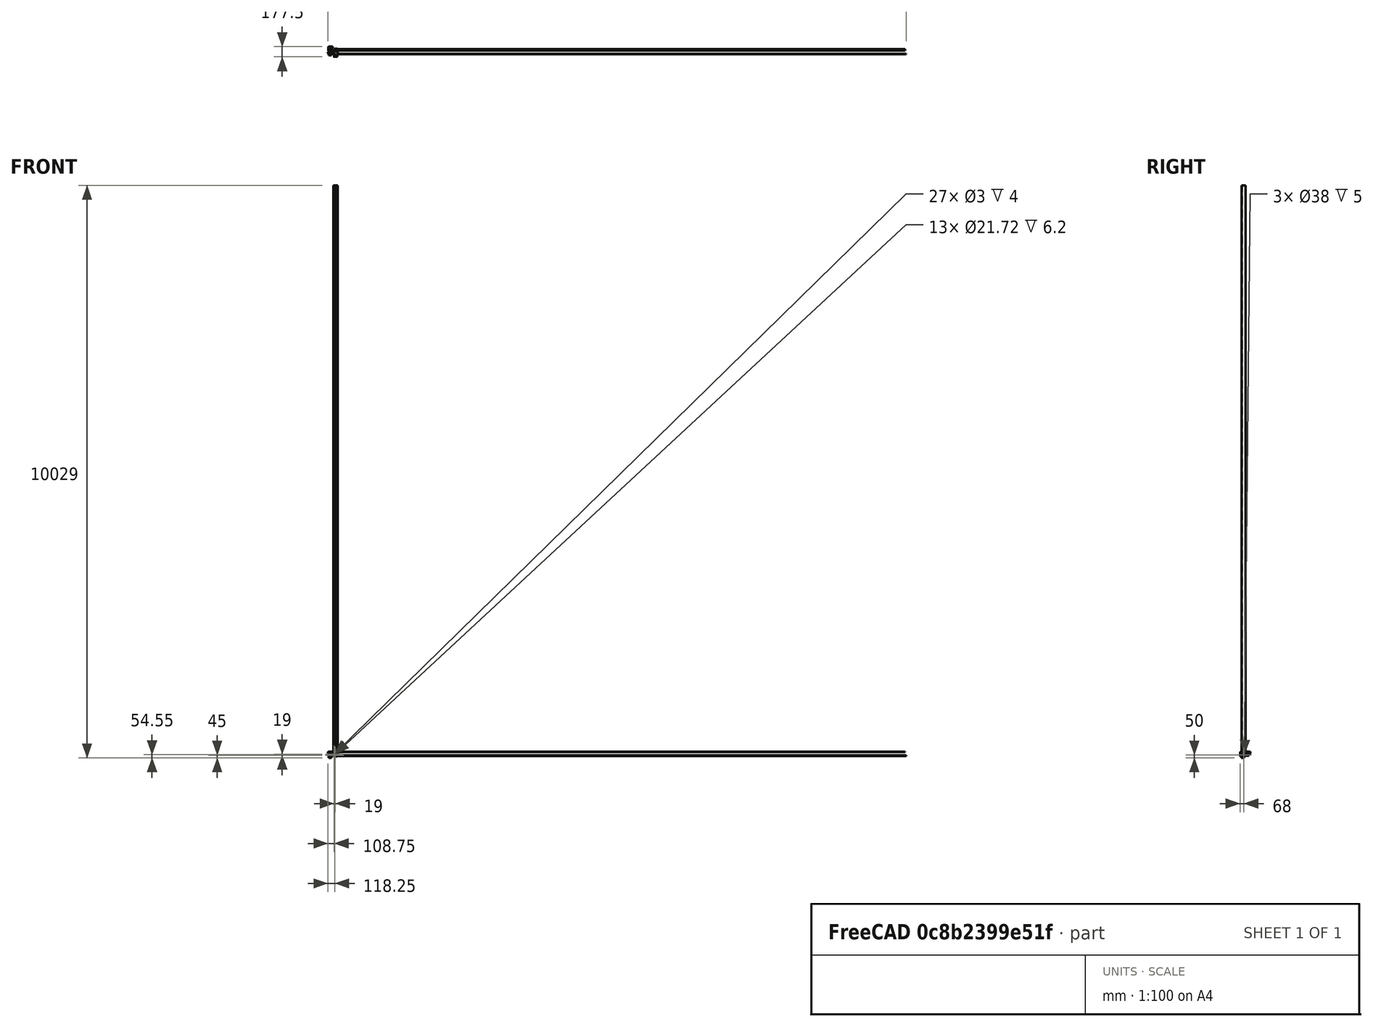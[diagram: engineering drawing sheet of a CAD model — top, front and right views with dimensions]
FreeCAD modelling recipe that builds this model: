
FCSTD DOCUMENT  (FreeCAD 0.15R4671 (Git))
Label: HexagonHotendFanShroud
License: All rights reserved
LicenseURL: http://en.wikipedia.org/wiki/All_rights_reserved
objects: Sketcher::SketchObject×30, Part::Feature×23, Mesh::Feature×20, PartDesign::Pocket×18, PartDesign::Pad×12, PartDesign::Fillet×10, Part::MultiFuse×1, PartDesign::Chamfer×1
note: 125 computed .brp shape members not serialized (recipe doc carries the construction recipe); baked Part::Feature solids carry a one-line shape summary decoded from their .brp

FEATURE [Part::Feature] Part__Feature  label="OB1515_45mm001"
  Placement = pos=(0,79.5,22.5) rot=(1,0,0;1.5708rad)
  shape: bbox 15 x 45 x 15 mm, 158 faces (baked)
FEATURE [Part::Feature] Part__Feature001  label="OB1515_45mm"
  Placement = pos=(7,93,-15) rot=(0,0,1;0.785398rad)
  shape: bbox 21.01 x 21.01 x 45 mm, 158 faces (baked)
FEATURE [Part::Feature] Part__Feature002  label="OB1515_45mm002"
  Placement = pos=(20.5,100,22.5) rot=(0.57735,0.57735,0.57735;2.0944rad)
  shape: bbox 45 x 15 x 15 mm, 158 faces (baked)
FEATURE [Part::Feature] Part__Feature003  label="NEMA17"
  Placement = pos=(36,64,2) rot=(0,0,1;0rad)
  shape: bbox 42.3 x 42.3 x 68 mm, 275 faces (baked)
FEATURE [Part::Feature] Part__Feature004  label="T5_Pulley"
  Placement = pos=(36,64,-4) rot=(0,0,1;0rad)
  shape: bbox 16 x 16 x 14.8 mm, 116 faces (baked)
FEATURE [Mesh::Feature] _08ZZ_Ball_Bearing  label="608ZZ_Ball_Bearing001"
  Placement = pos=(54.5,64,25.1) rot=(0,0,1;0rad)
FEATURE [Mesh::Feature] Spacer
  Placement = pos=(21.5,54,17.6) rot=(0,0,1;0rad)
FEATURE [Mesh::Feature] _mmRod_x100mm  label="8mmRod_x100mm"
  Placement = pos=(36,-64.5,-3.5) rot=(0,0,1;3.14159rad)
FEATURE [Part::Feature] Part__Feature005  label="TopCornerMotor"
  Placement = pos=(0,100,0) rot=(0,0,1;0rad)
  shape: bbox 69.55 x 77 x 28 mm, 82 faces (baked)
FEATURE [Part::Feature] Part__Feature006  label="TopRodHolder"
  Placement = pos=(0,100,2) rot=(0,0,1;0rad)
  shape: bbox 30.16 x 11.33 x 11.99 mm, 58 faces (baked)
FEATURE [Part::Feature] LM8UU_8mm_Linear_Bearing001
  Placement = pos=(36,-24.5,-3.5) rot=(0,0,1;1.5708rad)
  shape: bbox 15 x 24 x 15 mm, 34 faces (baked)
FEATURE [Mesh::Feature] _mmRod_x100mm001  label="8mmRod_x100mm001"
  Placement = pos=(66,7.5,1.5) rot=(0,0,1;1.5708rad)
FEATURE [Mesh::Feature] _mmRod_x100mm002  label="8mmRod_x100mm002"
  Placement = pos=(66,-32.5,1.5) rot=(0,0,1;1.5708rad)
FEATURE [Mesh::Feature] _0mmFan  label="40mmFan"
  Placement = pos=(102,-18,-36) rot=(-1,0,0;1.5708rad)
FEATURE [Mesh::Feature] HexHotEnd  label="HexHotEnd1"
  Placement = pos=(104,-57,-34) rot=(0,0,1;0rad)
FEATURE [Mesh::Feature] PNEUMATIC_NIPPLE
  Placement = pos=(111,-66,-3) rot=(0,-1,0;1.5708rad)
FEATURE [Part::Feature] Part__Feature015  label="AluAngle"
  Placement = pos=(0,5,-80) rot=(-1,0,0;1.5708rad)
  shape: bbox 50 x 50.8 x 50.8 mm, 9 faces (baked)
FEATURE [Mesh::Feature] _x10x4_FlangedBearing  label="5x10x4_FlangedBearing_BOTTOM"
  Placement = pos=(49,-6,16) rot=(-1,0,0;1.5708rad)
FEATURE [Mesh::Feature] _x10x4_FlangedBearing001  label="5x10x4_FlangedBearing_TOP"
  Placement = pos=(49,-6,12) rot=(1,0,0;1.5708rad)
FEATURE [Mesh::Feature] _x10x4_FlangedBearing002  label="5x10x4_FlangedBearing_BOTTOM001"
  Placement = pos=(49,-19,16) rot=(-1,0,0;1.5708rad)
FEATURE [Mesh::Feature] _x10x4_FlangedBearing003  label="5x10x4_FlangedBearing_TOP001"
  Placement = pos=(49,-19,12) rot=(1,0,0;1.5708rad)
FEATURE [Part::Feature] Part__Feature016  label="XCarrageBeltBlock"
  Placement = pos=(9,0,0) rot=(0,0,1;0rad)
  shape: bbox 56 x 22 x 10 mm, 113 faces (baked)
FEATURE [Part::Feature] Part__Feature017  label="LJ18A3"
  Placement = pos=(136,-57,-52) rot=(0,0,1;0rad)
  shape: bbox 17.85 x 17.85 x 79.1 mm, 11 faces (baked)
FEATURE [Mesh::Feature] HexNutStyle1_M002  label="HexNutStyle1_M006"
  Placement = pos=(50.3,7.15,-114) rot=(0,0,1;0.523599rad)
FEATURE [Mesh::Feature] HexNutStyle1_M003  label="HexNutStyle1_M007"
  Placement = pos=(50.3,20.15,-114) rot=(0,0,1;0.523599rad)
FEATURE [Part::Feature] Part__Feature018  label="YCarrage"
  shape: bbox 34.23 x 25.99 x 62.01 mm, 85 faces (baked)
FEATURE [Part::Feature] LM8UU_8mm_Linear_Bearing
  Placement = pos=(95,7.5,1.5) rot=(-1,0,0;1.5708rad)
  shape: bbox 24 x 15 x 15 mm, 34 faces (baked)
FEATURE [Part::Feature] LM8UU_8mm_Linear_Bearing002
  Placement = pos=(95,-32.5,1.5) rot=(-1,0,0;1.5708rad)
  shape: bbox 24 x 15 x 15 mm, 34 faces (baked)
FEATURE [Part::Feature] LM8UU_8mm_Linear_Bearing003
  Placement = pos=(123,7.5,1.5) rot=(-1,0,0;1.5708rad)
  shape: bbox 24 x 15 x 15 mm, 34 faces (baked)
FEATURE [Part::Feature] LM8UU_8mm_Linear_Bearing004
  Placement = pos=(123,-32.5,1.5) rot=(-1,0,0;1.5708rad)
  shape: bbox 24 x 15 x 15 mm, 34 faces (baked)
FEATURE [Mesh::Feature] MicroSwitch
  Placement = pos=(99,-12.5,-5) rot=(0,0,1;1.5708rad)
FEATURE [Part::Feature] Part__Feature019  label="XCarrageTop"
  shape: bbox 56 x 70.62 x 16.52 mm, 278 faces (baked)
FEATURE [Part::Feature] Part__Feature020  label="ChinaBlowerFan"
  shape: bbox 33.55 x 33.55 x 13 mm, 169 faces (baked)
FEATURE [Part::Feature] Part__Feature021  label="ChinaBlowerFan001"
  shape: bbox 40.62 x 40.6 x 19.6 mm, 81 faces (baked)
FEATURE [Part::MultiFuse] Fusion  label="ChinaBlowerFan002"
  Placement = pos=(114,-4,-13) rot=(0.707107,0.707107,0;3.14159rad)
  Shapes = -> [Part__Feature020,Part__Feature021]
FEATURE [Mesh::Feature] _0mmFan001  label="40mmFan001"
  Placement = pos=(141,-1,-23) rot=(0.57735,-0.57735,0.57735;4.18879rad)
FEATURE [Mesh::Feature] ALIEXPRESS_Aluhotend40mmFan
FEATURE [Mesh::Feature] Fan_25mm_x_10mm
  Placement = pos=(105.5,-31,-25.5) rot=(0,0.707107,0.707107;3.14159rad)
FEATURE [Mesh::Feature] HexHotEnd2
  Placement = pos=(104,-57,-34) rot=(0,0,1;0rad)
FEATURE [Part::Feature] Part__Feature022  label="Hexagon fanshroud"
  shape: bbox 25.5 x 25.5 x 18 mm, 35 faces (baked)
FEATURE [Mesh::Feature] hexagon_fan
  Placement = pos=(198.15,-46.7,56) rot=(0.57735,-0.57735,0.57735;2.0944rad)
FEATURE [Part::Feature] Part__Feature023  label="TempXCarrageBottom"
  shape: bbox 57.67 x 88 x 16.5 mm, 58 faces (baked)
FEATURE [Sketcher::SketchObject] Sketch
  Placement = pos=(0,0,-10.2) rot=(1,0,0;3.14159rad)
  sketch-geometry (4):
    g0: LineSegment StartX=93 StartY=70 StartZ=0 EndX=149 EndY=70 EndZ=0
    g1: LineSegment StartX=149 StartY=70 StartZ=0 EndX=149 EndY=-18 EndZ=0
    g2: LineSegment StartX=149 StartY=-18 StartZ=0 EndX=93 EndY=-18 EndZ=0
    g3: LineSegment StartX=93 StartY=-18 StartZ=0 EndX=93 EndY=70 EndZ=0
  constraints (8):
    c: Coincident(g0,g1)
    c: Coincident(g1,g2)
    c: Coincident(g2,g3)
    c: Coincident(g3,g0)
    c: Horizontal(g0)
    c: Horizontal(g2)
    c: Vertical(g1)
    c: Vertical(g3)
FEATURE [PartDesign::Pad] Pad
  Length = 3
  Length2 = 100
  Placement = pos=(0,0,-10.2) rot=(1,0,0;3.14159rad)
  Sketch = -> Sketch
  Type = 0
FEATURE [Sketcher::SketchObject] Sketch001
  Placement = pos=(0,0,-13.2) rot=(1,0,0;3.14159rad)
  Support = -> Pad [Face6]
  sketch-geometry (11):
    g0: LineSegment StartX=93 StartY=36 StartZ=0 EndX=118 EndY=36 EndZ=0
    g1: LineSegment StartX=118 StartY=36 StartZ=0 EndX=118 EndY=41 EndZ=0
    g2: LineSegment StartX=118 StartY=41 StartZ=0 EndX=114.5 EndY=62 EndZ=0
    g3: LineSegment StartX=93.5 StartY=62 StartZ=0 EndX=93 EndY=41 EndZ=0
    g4: LineSegment StartX=93 StartY=41 StartZ=0 EndX=93 EndY=36 EndZ=0
    g5: LineSegment StartX=114.5 StartY=62 StartZ=0 EndX=113 EndY=62 EndZ=0
    g6: LineSegment StartX=113 StartY=62 StartZ=0 EndX=113 EndY=52 EndZ=0
    g7: LineSegment StartX=113 StartY=52 StartZ=0 EndX=104 EndY=47 EndZ=0
    g8: LineSegment StartX=104 StartY=47 StartZ=0 EndX=95 EndY=52 EndZ=0
    g9: LineSegment StartX=95 StartY=52 StartZ=0 EndX=95 EndY=62 EndZ=0
    g10: LineSegment StartX=95 StartY=62 StartZ=0 EndX=93.5 EndY=62 EndZ=0
  constraints (16):
    c: Horizontal(g0)
    c: Coincident(g0,g1)
    c: Coincident(g1,g2)
    c: Coincident(g3,g4)
    c: Coincident(g4,g0)
    c: Coincident(g2,g5)
    c: Horizontal(g5)
    c: Coincident(g5,g6)
    c: Vertical(g6)
    c: Coincident(g6,g7)
    c: Coincident(g7,g8)
    c: Coincident(g8,g9)
    c: Vertical(g9)
    c: Coincident(g9,g10)
    c: Coincident(g10,g3)
    c: Horizontal(g10)
FEATURE [PartDesign::Pad] Pad001
  Length = 24.5
  Length2 = 100
  Placement = pos=(0,0,-10.2) rot=(1,0,0;3.14159rad)
  Sketch = -> Sketch001
  Type = 0
FEATURE [Sketcher::SketchObject] Sketch002
  Placement = pos=(93,0,-10.2) rot=(0.57735,0.57735,-0.57735;4.18879rad)
  Support = -> Pad001 [Face17]
  sketch-geometry (6):
    g0: LineSegment StartX=-63 StartY=23.5 StartZ=0 EndX=-62 EndY=23.5 EndZ=0
    g1: LineSegment StartX=-62 StartY=23.5 StartZ=0 EndX=-47 EndY=23.5 EndZ=0
    g2: LineSegment StartX=-47 StartY=23.5 StartZ=0 EndX=-41 EndY=25.5 EndZ=0
    g3: LineSegment StartX=-41 StartY=25.5 StartZ=0 EndX=-41 EndY=28 EndZ=0
    g4: LineSegment StartX=-41 StartY=28 StartZ=0 EndX=-63 EndY=28 EndZ=0
    g5: LineSegment StartX=-63 StartY=28 StartZ=0 EndX=-63 EndY=23.5 EndZ=0
  constraints (11):
    c: Horizontal(g0)
    c: Coincident(g0,g1)
    c: Horizontal(g1)
    c: Coincident(g1,g2)
    c: Coincident(g2,g3)
    c: Vertical(g3)
    c: Coincident(g3,g4)
    c: Horizontal(g4)
    c: Coincident(g4,g5)
    c: Coincident(g5,g0)
    c: Vertical(g5)
FEATURE [PartDesign::Pocket] Pocket
  Length = 5
  Placement = pos=(0,0,-10.2) rot=(1,0,0;3.14159rad)
  Sketch = -> Sketch002
  Type = 1
FEATURE [Sketcher::SketchObject] Sketch003
  Placement = pos=(0,-36,-10.2) rot=(-1,0,0;1.5708rad)
  Support = -> Pocket [Face7]
  sketch-geometry (1):
    g0: Circle CenterX=105.5 CenterY=15.25 CenterZ=0 NormalX=0 NormalY=0 NormalZ=1 Radius=10.8605
FEATURE [PartDesign::Pocket] Pocket001
  Length = 3
  Placement = pos=(0,0,-10.2) rot=(1,0,0;3.14159rad)
  Sketch = -> Sketch003
  Type = 0
FEATURE [Sketcher::SketchObject] Sketch004
  Placement = pos=(0,0,-10.2) rot=(0,0,1;0rad)
  Support = -> Pocket001 [Face4]
  sketch-geometry (7):
    g0: LineSegment StartX=94.75 StartY=-70.5 StartZ=0 EndX=94.75 EndY=-38.75 EndZ=0
    g1: LineSegment StartX=94.75 StartY=-38.75 StartZ=0 EndX=116.25 EndY=-38.75 EndZ=0
    g2: LineSegment StartX=116.25 StartY=-38.75 StartZ=0 EndX=116.5 EndY=-39 EndZ=0
    g3: LineSegment StartX=116.5 StartY=-39 StartZ=0 EndX=116.5 EndY=-41 EndZ=0
    g4: LineSegment StartX=116.5 StartY=-41 StartZ=0 EndX=113 EndY=-62 EndZ=0
    g5: LineSegment StartX=113 StartY=-62 StartZ=0 EndX=113 EndY=-70.5 EndZ=0
    g6: LineSegment StartX=113 StartY=-70.5 StartZ=0 EndX=94.75 EndY=-70.5 EndZ=0
  constraints (12):
    c: Vertical(g0)
    c: Horizontal(g1)
    c: Coincident(g1,g2)
    c: Coincident(g2,g3)
    c: Vertical(g3)
    c: Coincident(g3,g4)
    c: Coincident(g4,g5)
    c: Vertical(g5)
    c: Coincident(g5,g6)
    c: Horizontal(g6)
    c: Coincident(g0,g6)
    c: Coincident(g0,g1)
FEATURE [PartDesign::Pocket] Pocket002
  Length = 22.8
  Placement = pos=(0,0,-10.2) rot=(1,0,0;3.14159rad)
  Sketch = -> Sketch004
  Type = 0
FEATURE [PartDesign::Chamfer] Chamfer
  Base = -> Pocket002 [Edge60]
  Placement = pos=(0,0,-10.2) rot=(1,0,0;3.14159rad)
  Size = 3.2
FEATURE [PartDesign::Fillet] Fillet
  Base = -> Chamfer [Edge86,Edge76]
  Placement = pos=(0,0,-10.2) rot=(1,0,0;3.14159rad)
  Radius = 2
FEATURE [Sketcher::SketchObject] Sketch005
  Placement = pos=(0,0,-13.2) rot=(1,0,0;3.14159rad)
  Support = -> Fillet [Face4]
  sketch-geometry (8):
    g0: LineSegment StartX=92.5 StartY=41 StartZ=0 EndX=93.5 EndY=41 EndZ=0
    g1: LineSegment StartX=93.5 StartY=41 StartZ=0 EndX=93.5 EndY=62 EndZ=0
    g2: LineSegment StartX=93.5 StartY=62 StartZ=0 EndX=114.5 EndY=62 EndZ=0
    g3: LineSegment StartX=114.5 StartY=62 StartZ=0 EndX=118 EndY=41 EndZ=0
    g4: LineSegment StartX=118 StartY=41 StartZ=0 EndX=149.5 EndY=41 EndZ=0
    g5: LineSegment StartX=149.5 StartY=41 StartZ=0 EndX=149.5 EndY=70.25 EndZ=0
    g6: LineSegment StartX=149.5 StartY=70.25 StartZ=0 EndX=92.5 EndY=70.25 EndZ=0
    g7: LineSegment StartX=92.5 StartY=70.25 StartZ=0 EndX=92.5 EndY=41 EndZ=0
  constraints (14):
    c: Horizontal(g0)
    c: Coincident(g0,g1)
    c: Vertical(g1)
    c: Coincident(g1,g2)
    c: Horizontal(g2)
    c: Coincident(g2,g3)
    c: Coincident(g3,g4)
    c: Horizontal(g4)
    c: Coincident(g4,g5)
    c: Vertical(g5)
    c: Coincident(g5,g6)
    c: Horizontal(g6)
    c: Coincident(g6,g7)
    c: Coincident(g7,g0)
FEATURE [PartDesign::Pocket] Pocket003
  Length = 5
  Placement = pos=(0,0,-10.2) rot=(1,0,0;3.14159rad)
  Sketch = -> Sketch005
  Type = 0
FEATURE [Sketcher::SketchObject] Sketch006
  Placement = pos=(0,0,-10.2) rot=(0,0,1;0rad)
  Support = -> Pocket003 [Face11]
  sketch-geometry (7):
    g0: LineSegment StartX=93 StartY=-38.25 StartZ=0 EndX=93 EndY=-41 EndZ=0
    g1: LineSegment StartX=93 StartY=-41 StartZ=0 EndX=93.5 EndY=-62 EndZ=0
    g2: LineSegment StartX=93.5 StartY=-62 StartZ=0 EndX=94 EndY=-62 EndZ=0
    g3: LineSegment StartX=94 StartY=-62 StartZ=0 EndX=94 EndY=-44.25 EndZ=0
    g4: LineSegment StartX=94 StartY=-44.25 StartZ=0 EndX=116.75 EndY=-44.25 EndZ=0
    g5: LineSegment StartX=116.75 StartY=-44.25 StartZ=0 EndX=116.75 EndY=-38.25 EndZ=0
    g6: LineSegment StartX=116.75 StartY=-38.25 StartZ=0 EndX=93 EndY=-38.25 EndZ=0
  constraints (12):
    c: Vertical(g0)
    c: Coincident(g0,g1)
    c: Coincident(g1,g2)
    c: Horizontal(g2)
    c: Coincident(g2,g3)
    c: Coincident(g3,g4)
    c: Horizontal(g4)
    c: Coincident(g4,g5)
    c: Vertical(g5)
    c: Coincident(g5,g6)
    c: Horizontal(g6)
    c: Coincident(g0,g6)
FEATURE [PartDesign::Pad] Pad002
  Length = 3
  Length2 = 100
  Placement = pos=(0,0,-10.2) rot=(1,0,0;3.14159rad)
  Reversed = true
  Sketch = -> Sketch006
  Type = 0
FEATURE [Part::Feature] Pad002001  label="Pad003"
  shape: bbox 56 x 80 x 27.5 mm, 37 faces (baked)
FEATURE [Sketcher::SketchObject] Sketch007
  Placement = pos=(0,0,-13.2) rot=(1,0,0;3.14159rad)
  Support = -> Pad002001 [Face32]
  sketch-geometry (2):
    g0: Circle CenterX=107 CenterY=44.25 CenterZ=0 NormalX=0 NormalY=0 NormalZ=1 Radius=1.8
    g1: Circle CenterX=107 CenterY=44.25 CenterZ=0 NormalX=0 NormalY=0 NormalZ=1 Radius=3.25
  constraints (2):
    c: Radius(g0) = 1.8
    c: Coincident(g1,g0)
FEATURE [PartDesign::Pad] Pad002002
  Length = 3
  Length2 = 100
  Reversed = true
  Sketch = -> Sketch007
  Type = 0
FEATURE [Sketcher::SketchObject] Sketch008
  Placement = pos=(0,0,-13.2) rot=(1,0,0;3.14159rad)
  Support = -> Pad002002 [Face38]
  sketch-geometry (1):
    g0: Circle CenterX=107 CenterY=44.25 CenterZ=0 NormalX=0 NormalY=0 NormalZ=1 Radius=1.81
  constraints (1):
    c: Radius(g0) = 1.81
FEATURE [PartDesign::Pocket] Pocket004
  Length = 4
  Sketch = -> Sketch008
  Type = 0
FEATURE [PartDesign::Fillet] Fillet001
  Base = -> Pocket004 [Edge109,Edge105]
  Radius = 3
FEATURE [PartDesign::Fillet] Fillet002
  Base = -> Fillet001 [Edge42,Edge20]
  Radius = 2
FEATURE [Sketcher::SketchObject] Sketch009
  Placement = pos=(0,-36,0) rot=(0,0.707107,0.707107;3.14159rad)
  Support = -> Fillet002 [Face34]
  sketch-geometry (4):
    g0: Circle CenterX=-115 CenterY=-16 CenterZ=0 NormalX=0 NormalY=0 NormalZ=1 Radius=1.5
    g1: Circle CenterX=-96 CenterY=-16 CenterZ=0 NormalX=0 NormalY=0 NormalZ=1 Radius=1.5
    g2: Circle CenterX=-96 CenterY=-35 CenterZ=0 NormalX=0 NormalY=0 NormalZ=1 Radius=1.5
    g3: Circle CenterX=-115 CenterY=-35 CenterZ=0 NormalX=0 NormalY=0 NormalZ=1 Radius=1.5
  constraints (4):
    c: Radius(g0) = 1.5
    c: Radius(g1) = 1.5
    c: Radius(g2) = 1.5
    c: Radius(g3) = 1.5
FEATURE [PartDesign::Pocket] Pocket005
  Length = 4
  Sketch = -> Sketch009
  Type = 0
FEATURE [Sketcher::SketchObject] Sketch011
  Placement = pos=(0,0,-13.2) rot=(1,0,0;3.14159rad)
  Support = -> Pocket005 [Face27]
  sketch-geometry (4):
    g0: LineSegment StartX=138 StartY=-18 StartZ=0 EndX=134 EndY=-18 EndZ=0
    g1: LineSegment StartX=134 StartY=-18 StartZ=0 EndX=134 EndY=22 EndZ=0
    g2: LineSegment StartX=134 StartY=22 StartZ=0 EndX=138 EndY=22 EndZ=0
    g3: LineSegment StartX=138 StartY=22 StartZ=0 EndX=138 EndY=-18 EndZ=0
  constraints (8):
    c: Coincident(g0,g1)
    c: Coincident(g1,g2)
    c: Coincident(g2,g3)
    c: Coincident(g3,g0)
    c: Horizontal(g0)
    c: Horizontal(g2)
    c: Vertical(g1)
    c: Vertical(g3)
FEATURE [PartDesign::Pad] Pad002003
  Length = 37
  Length2 = 100
  Sketch = -> Sketch011
  Type = 0
FEATURE [Sketcher::SketchObject] Sketch012
  Placement = pos=(138,0,0) rot=(0.57735,0.57735,0.57735;2.0944rad)
  Support = -> Pad002003 [Face45]
  sketch-geometry (1):
    g0: Circle CenterX=-2 CenterY=-30 CenterZ=0 NormalX=0 NormalY=0 NormalZ=1 Radius=19
  constraints (1):
    c: Radius(g0) = 19
FEATURE [PartDesign::Pocket] Pocket006
  Length = 5
  Sketch = -> Sketch012
  Type = 0
FEATURE [Sketcher::SketchObject] Sketch013
  Placement = pos=(0,18,0) rot=(0,0.707107,0.707107;3.14159rad)
  Support = -> Pocket006 [Face15]
  sketch-geometry (6):
    g0: LineSegment StartX=-135 StartY=-50 StartZ=0 EndX=-93 EndY=-50 EndZ=0
    g1: LineSegment StartX=-93 StartY=-50 StartZ=0 EndX=-93 EndY=-39 EndZ=0
    g2: LineSegment StartX=-135 StartY=-12 StartZ=0 EndX=-135 EndY=-50 EndZ=0
    g3: LineSegment StartX=-93 StartY=-39 StartZ=0 EndX=-120 EndY=-39 EndZ=0
    g4: LineSegment StartX=-120 StartY=-39 StartZ=0 EndX=-126 EndY=-12 EndZ=0
    g5: LineSegment StartX=-126 StartY=-12 StartZ=0 EndX=-135 EndY=-12 EndZ=0
  constraints (11):
    c: Coincident(g0,g1)
    c: Coincident(g2,g0)
    c: Horizontal(g0)
    c: Vertical(g1)
    c: Vertical(g2)
    c: Coincident(g1,g3)
    c: Horizontal(g3)
    c: Coincident(g3,g4)
    c: Coincident(g4,g5)
    c: Horizontal(g5)
    c: Coincident(g2,g5)
FEATURE [PartDesign::Pad] Pad002004
  Length = 40
  Length2 = 100
  Reversed = true
  Sketch = -> Sketch013
  Type = 0
FEATURE [Sketcher::SketchObject] Sketch014
  Placement = pos=(93,0,0) rot=(0.57735,-0.57735,-0.57735;2.0944rad)
  Support = -> Pad002004 [Face57]
  sketch-geometry (5):
    g0: LineSegment StartX=24 StartY=-51.2126 StartZ=0 EndX=24 EndY=-41 EndZ=0
    g1: LineSegment StartX=24 StartY=-41 StartZ=0 EndX=22 EndY=-41 EndZ=0
    g2: LineSegment StartX=22 StartY=-41 StartZ=0 EndX=17 EndY=-50.2195 EndZ=0
    g3: LineSegment StartX=17 StartY=-50.2195 StartZ=0 EndX=17 EndY=-51.2126 EndZ=0
    g4: LineSegment StartX=17 StartY=-51.2126 StartZ=0 EndX=24 EndY=-51.2126 EndZ=0
  constraints (9):
    c: Vertical(g0)
    c: Coincident(g0,g1)
    c: Horizontal(g1)
    c: Coincident(g1,g2)
    c: Coincident(g2,g3)
    c: Vertical(g3)
    c: Coincident(g3,g4)
    c: Coincident(g4,g0)
    c: Horizontal(g4)
FEATURE [PartDesign::Pocket] Pocket007
  Length = 5
  Sketch = -> Sketch014
  Type = 1
FEATURE [PartDesign::Fillet] Fillet003
  Base = -> Pocket007 [Edge73]
  Radius = 25
FEATURE [Sketcher::SketchObject] Sketch015
  Placement = pos=(93,0,0) rot=(0.57735,-0.57735,-0.57735;2.0944rad)
  Support = -> Fillet003 [Face13]
  sketch-geometry (4):
    g0: LineSegment StartX=-21.7137 StartY=-49 StartZ=0 EndX=26 EndY=-49 EndZ=0
    g1: LineSegment StartX=26 StartY=-49 StartZ=0 EndX=26 EndY=-52 EndZ=0
    g2: LineSegment StartX=26 StartY=-52 StartZ=0 EndX=-21.7137 EndY=-52 EndZ=0
    g3: LineSegment StartX=-21.7137 StartY=-52 StartZ=0 EndX=-21.7137 EndY=-49 EndZ=0
  constraints (8):
    c: Coincident(g0,g1)
    c: Coincident(g1,g2)
    c: Coincident(g2,g3)
    c: Coincident(g3,g0)
    c: Horizontal(g0)
    c: Horizontal(g2)
    c: Vertical(g1)
    c: Vertical(g3)
FEATURE [PartDesign::Pocket] Pocket008
  Length = 41
  Sketch = -> Sketch015
  Type = 0
FEATURE [Sketcher::SketchObject] Sketch016
  Placement = pos=(0,0,-49) rot=(1,0,0;3.14159rad)
  Support = -> Pocket008 [Face2]
  sketch-geometry (5):
    g0: ArcOfCircle CenterX=117.001 CenterY=6 CenterZ=0 NormalX=0 NormalY=0 NormalZ=1 Radius=21.0014 StartAngle=3.14159 EndAngle=4.72394
    g1: LineSegment StartX=96 StartY=6 StartZ=0 EndX=96 EndY=23.1942 EndZ=0
    g2: LineSegment StartX=96 StartY=23.1942 StartZ=0 EndX=134 EndY=23.1942 EndZ=0
    g3: LineSegment StartX=134 StartY=23.1942 StartZ=0 EndX=134 EndY=-15 EndZ=0
    g4: LineSegment StartX=134 StartY=-15 StartZ=0 EndX=117.244 EndY=-15 EndZ=0
  constraints (8):
    c: Tangent(g0,g1) = 1.5708
    c: Coincident(g1,g2)
    c: Horizontal(g2)
    c: Coincident(g2,g3)
    c: Vertical(g3)
    c: Coincident(g3,g4)
    c: Coincident(g4,g0)
    c: Horizontal(g4)
FEATURE [PartDesign::Pocket] Pocket009
  Length = 8
  Sketch = -> Sketch016
  Type = 0
FEATURE [Sketcher::SketchObject] Sketch017
  Placement = pos=(0,-22,0) rot=(1,0,0;1.5708rad)
  Support = -> Pocket009 [Face18]
  sketch-geometry (5):
    g0: LineSegment StartX=134 StartY=-13 StartZ=0 EndX=128 EndY=-13 EndZ=0
    g1: LineSegment StartX=128 StartY=-13 StartZ=0 EndX=122 EndY=-41 EndZ=0
    g2: LineSegment StartX=122 StartY=-41 StartZ=0 EndX=122 EndY=-42 EndZ=0
    g3: LineSegment StartX=122 StartY=-42 StartZ=0 EndX=134 EndY=-42 EndZ=0
    g4: LineSegment StartX=134 StartY=-42 StartZ=0 EndX=134 EndY=-13 EndZ=0
  constraints (7):
    c: Coincident(g0,g1)
    c: Coincident(g1,g2)
    c: Coincident(g2,g3)
    c: Horizontal(g3)
    c: Coincident(g3,g4)
    c: Vertical(g4)
    c: Coincident(g0,g4)
FEATURE [PartDesign::Pocket] Pocket010
  Length = 37
  Sketch = -> Sketch017
  Type = 0
FEATURE [PartDesign::Fillet] Fillet004
  Base = -> Pocket010 [Edge164]
  Radius = 6
FEATURE [PartDesign::Fillet] Fillet005
  Base = -> Fillet004 [Edge42]
  Radius = 4
FEATURE [PartDesign::Fillet] Fillet006
  Base = -> Fillet005 [Edge10]
  Radius = 3
FEATURE [Sketcher::SketchObject] Sketch018
  Placement = pos=(149,0,0) rot=(0.57735,0.57735,0.57735;2.0944rad)
  Support = -> Fillet006 [Face30]
  sketch-geometry (1):
    g0: Circle CenterX=-2 CenterY=-30 CenterZ=0 NormalX=0 NormalY=0 NormalZ=1 Radius=19.1
  constraints (1):
    c: Radius(g0) = 19.1
FEATURE [PartDesign::Pocket] Pocket011
  Length = 15
  Sketch = -> Sketch018
  Type = 0
FEATURE [Sketcher::SketchObject] Sketch019
  Placement = pos=(0,0,-49) rot=(1,0,0;3.14159rad)
  Support = -> Pocket011 [Face15]
  sketch-geometry (5):
    g0: LineSegment StartX=93 StartY=17.75 StartZ=0 EndX=138 EndY=17.75 EndZ=0
    g1: LineSegment StartX=138 StartY=17.75 StartZ=0 EndX=138 EndY=-18.0159 EndZ=0
    g2: LineSegment StartX=138 StartY=-18.0159 StartZ=0 EndX=117.75 EndY=-18.0159 EndZ=0
    g3: LineSegment StartX=93 StartY=17.75 StartZ=0 EndX=93 EndY=6.75 EndZ=0
    g4: ArcOfCircle CenterX=117.884 CenterY=6.86846 CenterZ=0 NormalX=0 NormalY=0 NormalZ=1 Radius=24.8847 StartAngle=3.14635 EndAngle=4.70698
  constraints (9):
    c: Horizontal(g0)
    c: Coincident(g0,g1)
    c: Vertical(g1)
    c: Coincident(g1,g2)
    c: Horizontal(g2)
    c: Coincident(g3,g0)
    c: Vertical(g3)
    c: Coincident(g4,g2)
    c: Coincident(g4,g3)
FEATURE [PartDesign::Pad] Pad002005
  Length = 2
  Length2 = 100
  Sketch = -> Sketch019
  Type = 0
FEATURE [Sketcher::SketchObject] Sketch020
  Placement = pos=(93,0,0) rot=(0.57735,-0.57735,-0.57735;2.0944rad)
  Support = -> Pad002005 [Face90]
  sketch-geometry (5):
    g0: LineSegment StartX=22.25 StartY=-39 StartZ=0 EndX=22 EndY=-39 EndZ=0
    g1: LineSegment StartX=22 StartY=-39 StartZ=0 EndX=17.5 EndY=-49 EndZ=0
    g2: LineSegment StartX=17.5 StartY=-49 StartZ=0 EndX=17.5 EndY=-51 EndZ=0
    g3: LineSegment StartX=17.5 StartY=-51 StartZ=0 EndX=22.25 EndY=-51 EndZ=0
    g4: LineSegment StartX=22.25 StartY=-51 StartZ=0 EndX=22.25 EndY=-39 EndZ=0
  constraints (9):
    c: Horizontal(g0)
    c: Coincident(g0,g1)
    c: Coincident(g1,g2)
    c: Vertical(g2)
    c: Coincident(g2,g3)
    c: Horizontal(g3)
    c: Coincident(g3,g4)
    c: Coincident(g4,g0)
    c: Vertical(g4)
FEATURE [Sketcher::SketchObject] Sketch021
  Placement = pos=(0,-22,0) rot=(1,0,0;1.5708rad)
  Support = -> Pad002005 [Face26]
  sketch-geometry (6):
    g0: LineSegment StartX=138 StartY=-13 StartZ=0 EndX=125.75 EndY=-13 EndZ=0
    g1: LineSegment StartX=125.75 StartY=-13 StartZ=0 EndX=120 EndY=-39 EndZ=0
    g2: LineSegment StartX=120 StartY=-39 StartZ=0 EndX=112 EndY=-39 EndZ=0
    g3: LineSegment StartX=112 StartY=-39 StartZ=0 EndX=112 EndY=-51 EndZ=0
    g4: LineSegment StartX=112 StartY=-51 StartZ=0 EndX=138 EndY=-51 EndZ=0
    g5: LineSegment StartX=138 StartY=-51 StartZ=0 EndX=138 EndY=-13 EndZ=0
  constraints (11):
    c: Horizontal(g0)
    c: Coincident(g0,g1)
    c: Coincident(g1,g2)
    c: Horizontal(g2)
    c: Coincident(g2,g3)
    c: Vertical(g3)
    c: Coincident(g3,g4)
    c: Horizontal(g4)
    c: Coincident(g4,g5)
    c: Coincident(g5,g0)
    c: Vertical(g5)
FEATURE [PartDesign::Pad] Pad002006
  Length = 3
  Length2 = 100
  Sketch = -> Sketch021
  Type = 0
FEATURE [PartDesign::Pad] Pad002007
  Length = 45
  Length2 = 100
  Reversed = true
  Sketch = -> Sketch020
  Type = 0
FEATURE [Sketcher::SketchObject] Sketch022
  Placement = pos=(93,0,0) rot=(0.57735,-0.57735,-0.57735;2.0944rad)
  Support = -> Pad002007 [Face90]
  sketch-geometry (4):
    g0: LineSegment StartX=26 StartY=-52 StartZ=0 EndX=16.1404 EndY=-52 EndZ=0
    g1: LineSegment StartX=16.1404 StartY=-52 StartZ=0 EndX=22 EndY=-39 EndZ=0
    g2: LineSegment StartX=22 StartY=-39 StartZ=0 EndX=26 EndY=-39 EndZ=0
    g3: LineSegment StartX=26 StartY=-39 StartZ=0 EndX=26 EndY=-52 EndZ=0
  constraints (7):
    c: Horizontal(g0)
    c: Coincident(g0,g1)
    c: Coincident(g1,g2)
    c: Horizontal(g2)
    c: Coincident(g2,g3)
    c: Coincident(g3,g0)
    c: Vertical(g3)
FEATURE [Sketcher::SketchObject] Sketch023
  Placement = pos=(0,-22.25,0) rot=(1,0,0;1.5708rad)
  Support = -> Pad002007 [Face1]
  sketch-geometry (4):
    g0: LineSegment StartX=138 StartY=-39.25 StartZ=0 EndX=138 EndY=-13 EndZ=0
    g1: LineSegment StartX=138 StartY=-13 StartZ=0 EndX=125.75 EndY=-13 EndZ=0
    g2: LineSegment StartX=125.75 StartY=-13 StartZ=0 EndX=120 EndY=-39.25 EndZ=0
    g3: LineSegment StartX=120 StartY=-39.25 StartZ=0 EndX=138 EndY=-39.25 EndZ=0
  constraints (7):
    c: Vertical(g0)
    c: Coincident(g0,g1)
    c: Horizontal(g1)
    c: Coincident(g1,g2)
    c: Coincident(g2,g3)
    c: PointOnObject(g3,g0)
    c: Horizontal(g3)
FEATURE [PartDesign::Pad] Pad002008
  Length = 2
  Length2 = 100
  Reversed = true
  Sketch = -> Sketch023
  Type = 0
FEATURE [PartDesign::Pocket] Pocket012
  Length = 19
  Sketch = -> Sketch022
  Type = 0
FEATURE [Sketcher::SketchObject] Sketch024
  Placement = pos=(112,0,0) rot=(0.57735,-0.57735,-0.57735;2.0944rad)
  Support = -> Pocket012 [Face2]
  sketch-geometry (6):
    g0: LineSegment StartX=22.75 StartY=-38.5 StartZ=0 EndX=22 EndY=-38.5 EndZ=0
    g1: LineSegment StartX=22 StartY=-38.5 StartZ=0 EndX=22 EndY=-42 EndZ=0
    g2: LineSegment StartX=22 StartY=-42 StartZ=0 EndX=18.25 EndY=-51.25 EndZ=0
    g3: LineSegment StartX=18.25 StartY=-51.25 StartZ=0 EndX=18.25 EndY=-51.75 EndZ=0
    g4: LineSegment StartX=18.25 StartY=-51.75 StartZ=0 EndX=22.75 EndY=-51.75 EndZ=0
    g5: LineSegment StartX=22.75 StartY=-51.75 StartZ=0 EndX=22.75 EndY=-38.5 EndZ=0
  constraints (11):
    c: Horizontal(g0)
    c: Coincident(g0,g1)
    c: Vertical(g1)
    c: Coincident(g1,g2)
    c: Coincident(g2,g3)
    c: Vertical(g3)
    c: Coincident(g3,g4)
    c: Horizontal(g4)
    c: Coincident(g4,g5)
    c: Coincident(g5,g0)
    c: Vertical(g5)
FEATURE [PartDesign::Pocket] Pocket013
  Length = 5
  Sketch = -> Sketch024
  Type = 1
FEATURE [Sketcher::SketchObject] Sketch025
  Placement = pos=(138,0,0) rot=(0.57735,0.57735,0.57735;2.0944rad)
  Support = -> Pocket013 [Face14]
  sketch-geometry (4):
    g0: LineSegment StartX=-22 StartY=-40 StartZ=0 EndX=-21 EndY=-40 EndZ=0
    g1: LineSegment StartX=-21 StartY=-40 StartZ=0 EndX=-21 EndY=-12.92 EndZ=0
    g2: LineSegment StartX=-21 StartY=-12.92 StartZ=0 EndX=-22 EndY=-12.92 EndZ=0
    g3: LineSegment StartX=-22 StartY=-12.92 StartZ=0 EndX=-22 EndY=-40 EndZ=0
  constraints (8):
    c: Coincident(g0,g1)
    c: Coincident(g1,g2)
    c: Coincident(g2,g3)
    c: Coincident(g3,g0)
    c: Horizontal(g0)
    c: Horizontal(g2)
    c: Vertical(g1)
    c: Vertical(g3)
FEATURE [PartDesign::Pad] Pad002009
  Length = 22
  Length2 = 100
  Reversed = true
  Sketch = -> Sketch025
  Type = 0
FEATURE [Sketcher::SketchObject] Sketch026
  Placement = pos=(0,-21,0) rot=(0,0.707107,0.707107;3.14159rad)
  Support = -> Pad002009 [Face27]
  sketch-geometry (11):
    g0: LineSegment StartX=-115.74 StartY=-13.2067 StartZ=0 EndX=-125.75 EndY=-13.2067 EndZ=0
    g1: LineSegment StartX=-125.75 StartY=-13.2067 StartZ=0 EndX=-120.679 EndY=-35.8838 EndZ=0
    g2: LineSegment StartX=-120.679 StartY=-35.8838 StartZ=0 EndX=-120.25 EndY=-36.9498 EndZ=0
    g3: LineSegment StartX=-120.25 StartY=-36.9498 StartZ=0 EndX=-119.584 EndY=-37.843 EndZ=0
    g4: LineSegment StartX=-119.584 StartY=-37.843 StartZ=0 EndX=-118.75 EndY=-38.448 EndZ=0
    g5: LineSegment StartX=-118.75 StartY=-38.448 StartZ=0 EndX=-118.375 EndY=-38.6372 EndZ=0
    g6: LineSegment StartX=-118.375 StartY=-38.6372 StartZ=0 EndX=-117.599 EndY=-38.8897 EndZ=0
    g7: LineSegment StartX=-117.599 StartY=-38.8897 StartZ=0 EndX=-117.25 EndY=-38.935 EndZ=0
    g8: LineSegment StartX=-117.25 StartY=-38.935 StartZ=0 EndX=-116.75 EndY=-39 EndZ=0
    g9: LineSegment StartX=-116.75 StartY=-39 StartZ=0 EndX=-115.74 EndY=-39 EndZ=0
    g10: LineSegment StartX=-115.74 StartY=-39 StartZ=0 EndX=-115.74 EndY=-13.2067 EndZ=0
  constraints (14):
    c: Horizontal(g0)
    c: Coincident(g0,g1)
    c: Coincident(g1,g2)
    c: Coincident(g2,g3)
    c: Coincident(g3,g4)
    c: Coincident(g4,g5)
    c: Coincident(g5,g6)
    c: Coincident(g6,g7)
    c: Coincident(g7,g8)
    c: Coincident(g8,g9)
    c: Horizontal(g9)
    c: Coincident(g9,g10)
    c: Coincident(g10,g0)
    c: Vertical(g10)
FEATURE [PartDesign::Pocket] Pocket014
  Length = 5
  Sketch = -> Sketch026
  Type = 0
FEATURE [Sketcher::SketchObject] Sketch027
  Placement = pos=(0,0,-13.2) rot=(1,0,0;3.14159rad)
  Support = -> Pocket014 [Face42]
  sketch-geometry (4):
    g0: LineSegment StartX=150 StartY=22 StartZ=0 EndX=138 EndY=22 EndZ=0
    g1: LineSegment StartX=138 StartY=22 StartZ=0 EndX=138 EndY=-19 EndZ=0
    g2: LineSegment StartX=138 StartY=-19 StartZ=0 EndX=150 EndY=-19 EndZ=0
    g3: LineSegment StartX=150 StartY=-19 StartZ=0 EndX=150 EndY=22 EndZ=0
  constraints (8):
    c: Coincident(g0,g1)
    c: Coincident(g1,g2)
    c: Coincident(g2,g3)
    c: Coincident(g3,g0)
    c: Horizontal(g0)
    c: Horizontal(g2)
    c: Vertical(g1)
    c: Vertical(g3)
FEATURE [PartDesign::Pocket] Pocket015
  Length = 5
  Sketch = -> Sketch027
  Type = 0
FEATURE [Sketcher::SketchObject] Sketch028
  Placement = pos=(0,0,-51) rot=(1,0,0;3.14159rad)
  Support = -> Pocket015 [Face8]
  sketch-geometry (6):
    g0: LineSegment StartX=118 StartY=22 StartZ=0 EndX=118 EndY=42 EndZ=0
    g1: LineSegment StartX=118 StartY=42 StartZ=0 EndX=157.22 EndY=42 EndZ=0
    g2: LineSegment StartX=157.22 StartY=42 StartZ=0 EndX=157.22 EndY=-28.296 EndZ=0
    g3: LineSegment StartX=157.22 StartY=-28.296 StartZ=0 EndX=78.471 EndY=-28.296 EndZ=0
    g4: LineSegment StartX=78.471 StartY=-28.296 StartZ=0 EndX=78.471 EndY=22 EndZ=0
    g5: LineSegment StartX=78.471 StartY=22 StartZ=0 EndX=118 EndY=22 EndZ=0
  constraints (11):
    c: Vertical(g0)
    c: Coincident(g0,g1)
    c: Horizontal(g1)
    c: Coincident(g1,g2)
    c: Vertical(g2)
    c: Coincident(g2,g3)
    c: Horizontal(g3)
    c: Coincident(g3,g4)
    c: Vertical(g4)
    c: Coincident(g4,g5)
    c: Horizontal(g5)
FEATURE [PartDesign::Pocket] Pocket016
  Length = 5
  Sketch = -> Sketch028
  Type = 1
FEATURE [Sketcher::SketchObject] Sketch029
  Placement = pos=(0,0,-13.2) rot=(1,0,0;3.14159rad)
  Support = -> Pocket016 [Face24]
  sketch-geometry (2):
    g0: Circle CenterX=96.46 CenterY=22 CenterZ=0 NormalX=0 NormalY=0 NormalZ=1 Radius=3.46164
    g1: Circle CenterX=114.5 CenterY=22 CenterZ=0 NormalX=0 NormalY=0 NormalZ=1 Radius=3.46164
  constraints (2):
    c: Radius(g0) = 3.46164
    c: Radius(g1) = 3.46164
FEATURE [PartDesign::Pad] Pad002010
  Length = 3
  Length2 = 100
  Reversed = true
  Sketch = -> Sketch029
  Type = 0
FEATURE [Sketcher::SketchObject] Sketch030
  Placement = pos=(0,0,-13.2) rot=(1,0,0;3.14159rad)
  Support = -> Pad002010 [Face52]
  sketch-geometry (2):
    g0: Circle CenterX=96.5 CenterY=22 CenterZ=0 NormalX=0 NormalY=0 NormalZ=1 Radius=1.8
    g1: Circle CenterX=114.5 CenterY=22 CenterZ=0 NormalX=0 NormalY=0 NormalZ=1 Radius=1.8
  constraints (2):
    c: Radius(g0) = 1.8
    c: Radius(g1) = 1.8
FEATURE [PartDesign::Pocket] Pocket017
  Length = 5
  Sketch = -> Sketch030
  Type = 0
FEATURE [PartDesign::Fillet] Fillet007
  Base = -> Pocket017 [Edge87,Edge31]
  Radius = 2
FEATURE [PartDesign::Fillet] Fillet008
  Base = -> Fillet007 [Edge48]
  Radius = 1
FEATURE [PartDesign::Fillet] Fillet009
  Base = -> Fillet008 [Edge44]
  Radius = 1
FEATURE [Part::Feature] Fillet009001  label="HexagonHotendFanShroud"
  shape: bbox 25.53 x 43.75 x 27.5 mm, 64 faces (baked)
